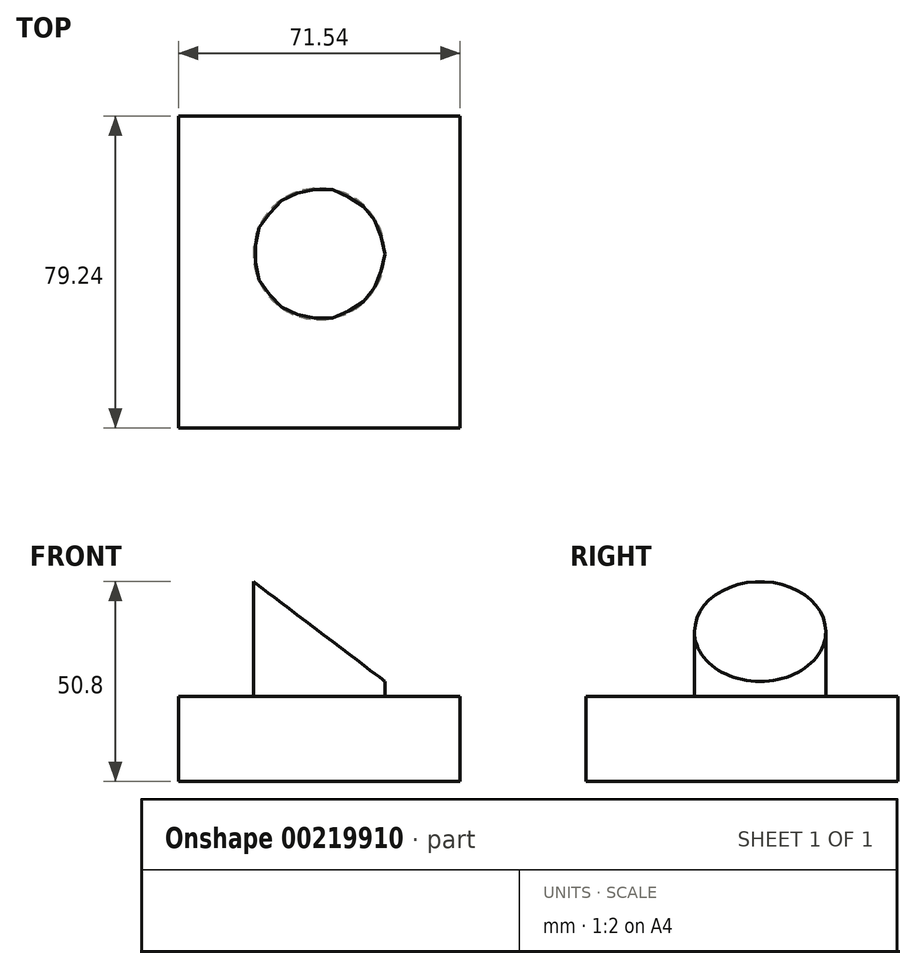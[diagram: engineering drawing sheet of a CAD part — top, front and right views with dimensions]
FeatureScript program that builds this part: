
annotation { "Feature Type Name" : "Feature", "Feature Type Description" : "" }
export const myFeature = defineFeature(function(context is Context, id is Id, definition is map)
    precondition{}
    {
        {
            var Q0;
            Q0=qCreatedBy(makeId("Top.planeOp"),FACE);
            var sketch = newSketch(context, id + "F0", { "sketchPlane" : qUnion([Q0])});
            skCircle(sketch, "E0", {"center": v(0, 0) * mm, "radius": 16.73 * mm});
            skLineSegment(sketch, "E1.bottom", {"start": v(0, 35) * mm, "end": v(-35.77, 35) * mm});
            skLineSegment(sketch, "E1.top", {"start": v(0, -44.24) * mm, "end": v(-35.77, -44.24) * mm});
            skLineSegment(sketch, "E1.left", {"start": v(0, 35) * mm, "end": v(0, -44.24) * mm});
            skLineSegment(sketch, "E1.right", {"start": v(-35.77, 35) * mm, "end": v(-35.77, -44.24) * mm});
            skLineSegment(sketch, "E2.MirrorCS", {"start": v(0, -44.24) * mm, "end": v(35.77, -44.24) * mm});
            skLineSegment(sketch, "E3.MirrorCS", {"start": v(35.77, 35) * mm, "end": v(35.77, -44.24) * mm});
            skLineSegment(sketch, "E4.MirrorCS", {"start": v(0, 35) * mm, "end": v(35.77, 35) * mm});
            skSolve(sketch);
        }
        {
            var Q0;
            {var subQ0=sQuery(id+"F0.wireOp",EDGE,"E1.left");var subQ1=sQuery(id+"F0.wireOp",EDGE,"E0");var subQ2=makeQuery(id+"F0.imprint","INTERSECT",VERTEX,{"disambiguationData":[OD(0.0)],"derivedFrom":[subQ1,subQ0]});Q0=makeQuery(id+"F0.imprint","IMPRINT",FACE,{"disambiguationData":[TD([[makeQuery(id+"F0.imprint","IMPRINT",EDGE,{"disambiguationData":[TD([[subQ2,-1.0]])],"derivedFrom":subQ1}),1.0]])]});}
            var Q1;
            {var subQ0=sQuery(id+"F0.wireOp",EDGE,"E1.left");var subQ1=sQuery(id+"F0.wireOp",EDGE,"E0");var subQ2=makeQuery(id+"F0.imprint","INTERSECT",VERTEX,{"disambiguationData":[OD(0.0)],"derivedFrom":[subQ1,subQ0]});Q1=makeQuery(id+"F0.imprint","IMPRINT",FACE,{"disambiguationData":[TD([[makeQuery(id+"F0.imprint","IMPRINT",EDGE,{"disambiguationData":[TD([[subQ2,1.0]])],"derivedFrom":subQ1}),1.0]])]});}
            extrude(context, id + "F1", {"entities" : qUnion([Q0, Q1]), "depth" : 50.8 * mm});
        }
        {
            var Q0;
            {var subQ1=sQuery(id+"F0.wireOp",EDGE,"E1.bottom");Q0=makeQuery(id+"F0.imprint","IMPRINT",FACE,{"disambiguationData":[TD([[makeQuery(id+"F0.imprint","IMPRINT",EDGE,{"derivedFrom":subQ1}),1.0]])]});}
            var Q1;
            {var subQ0=sQuery(id+"F0.wireOp",EDGE,"E2.MirrorCS");Q1=makeQuery(id+"F0.imprint","IMPRINT",FACE,{"disambiguationData":[TD([[makeQuery(id+"F0.imprint","IMPRINT",EDGE,{"derivedFrom":subQ0}),1.0]])]});}
            extrude(context, id + "F2", {"entities" : qUnion([Q0, Q1]), "operationType" : NewBodyOperationType.ADD, "depth" : 21.59 * mm});
        }
        {
            var Q0;
            Q0=makeQuery(id+"F2.opExtrude","SWEPT_FACE",FACE,{"disambiguationData":[OSD([sQuery(id+"F0.wireOp",EDGE,"E1.top"),sQuery(id+"F0.wireOp",EDGE,"E2.MirrorCS")])]});
            var sketch = newSketch(context, id + "F3", { "sketchPlane" : qUnion([Q0])});
            skLineSegment(sketch, "E5.0", {"start": v(-16.73, 50.8) * mm, "end": v(16.73, 50.8) * mm});
            skLineSegment(sketch, "E6", {"start": v(16.73, 50.8) * mm, "end": v(16.73, 25.4) * mm});
            skLineSegment(sketch, "E7", {"start": v(16.73, 25.4) * mm, "end": v(-16.73, 50.8) * mm});
            skSolve(sketch);
        }
        {
            var Q0;
            Q0 = qSketchRegion(id + "F3", true);
            extrude(context, id + "F4", {"entities" : qUnion([Q0]), "operationType" : NewBodyOperationType.REMOVE, "endBound" : BoundingType.THROUGH_ALL, "oppositeDirection" : true, "depth" : 25.4 * mm});
        }
    });
